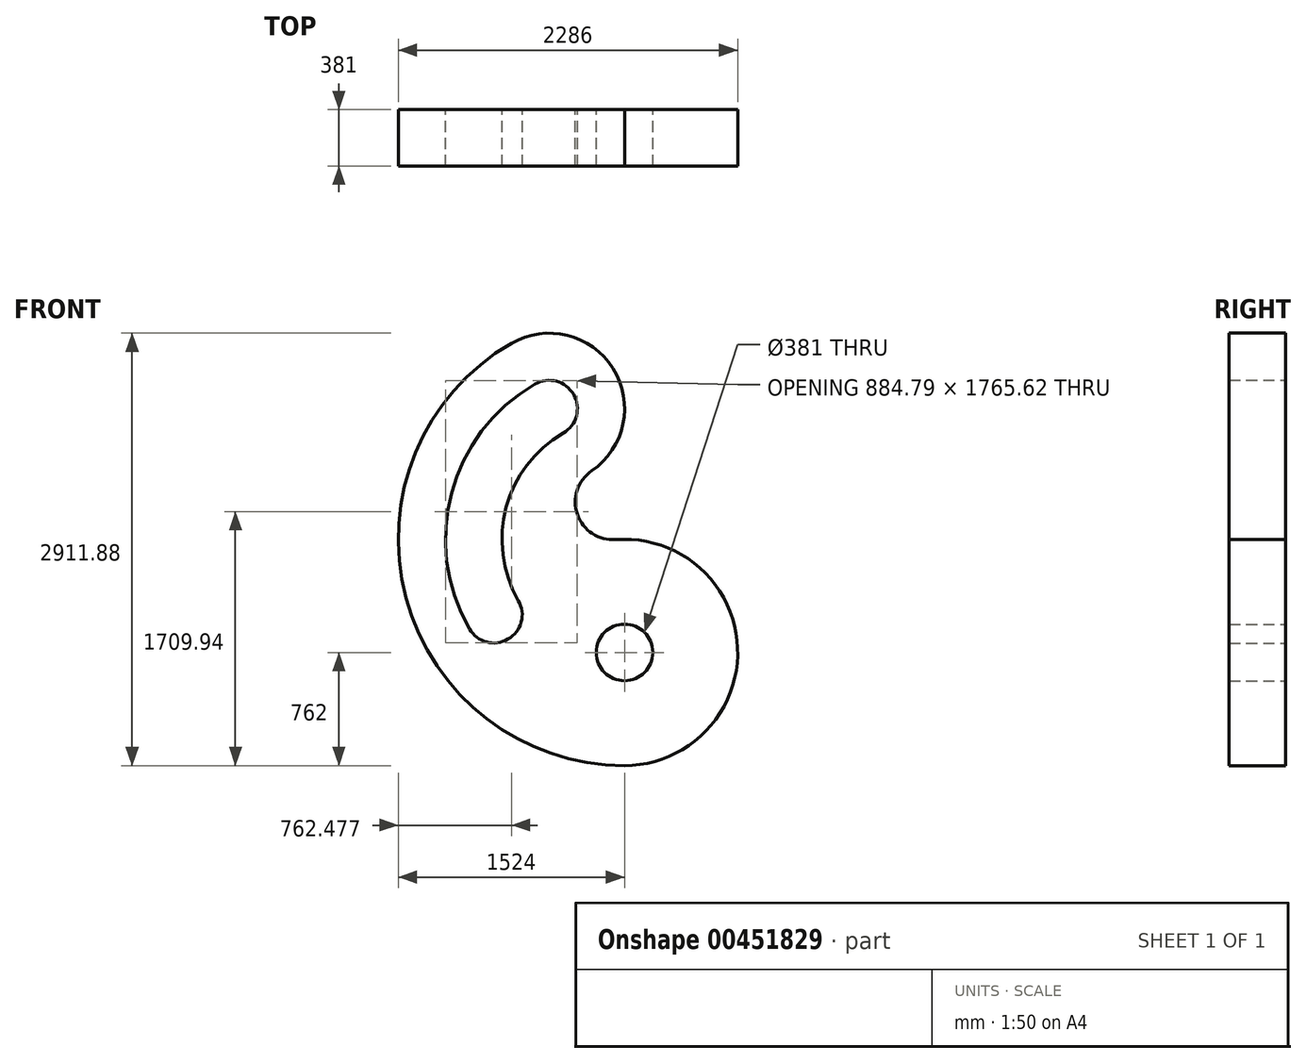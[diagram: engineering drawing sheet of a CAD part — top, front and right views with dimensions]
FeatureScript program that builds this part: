
annotation { "Feature Type Name" : "Feature", "Feature Type Description" : "" }
export const myFeature = defineFeature(function(context is Context, id is Id, definition is map)
    precondition{}
    {
        {
            var Q0;
            Q0=qCreatedBy(makeId("Front.planeOp"),FACE);
            var sketch = newSketch(context, id + "F0", { "sketchPlane" : qUnion([Q0])});
            skCircle(sketch, "E0", {"center": v(0, 0) * mm, "radius": 190.5 * mm});
            skArc(sketch, "E1", {"start": v(-412.75, 1476.9) * mm, "mid": v(-343.02, 1737.13) * mm, "end": v(-603.25, 1806.86) * mm});
            skArc(sketch, "E2", {"start": v(-1044.86, 158.75) * mm, "mid": v(-784.63, 89.02) * mm, "end": v(-714.9, 349.25) * mm});
            skArc(sketch, "E3.0", {"start": v(-603.25, 1806.86) * mm, "mid": v(-1165.39, 1074.27) * mm, "end": v(-1044.86, 158.75) * mm});
            skArc(sketch, "E4.0", {"start": v(-412.75, 1476.9) * mm, "mid": v(-797.37, 975.66) * mm, "end": v(-714.9, 349.25) * mm});
            skArc(sketch, "E5", {"start": v(-762, 2081.82) * mm, "mid": v(-1472.07, 367.56) * mm, "end": v(0, -762) * mm});
            skArc(sketch, "E6", {"start": v(-221.11, 1222.65) * mm, "mid": v(-317.27, 928.72) * mm, "end": v(-58.25, 759.77) * mm});
            skArc(sketch, "E7.trimOffspring", {"start": v(0, -762) * mm, "mid": v(761.44, 29.15) * mm, "end": v(-58.25, 759.77) * mm});
            skArc(sketch, "E8.trimOffspring", {"start": v(-221.11, 1222.65) * mm, "mid": v(-78.1, 1912.52) * mm, "end": v(-762, 2081.82) * mm});
            skSolve(sketch);
        }
        {
            var Q0;
            Q0=makeQuery(id+"F0.imprint","IMPRINT",FACE,{"disambiguationData":[TD([[makeQuery(id+"F0.imprint","IMPRINT",EDGE,{"derivedFrom":sQuery(id+"F0.wireOp",EDGE,"E0")}),-1.0]])]});
            extrude(context, id + "F1", {"entities" : qUnion([Q0]), "depth" : 381 * mm});
        }
    });
